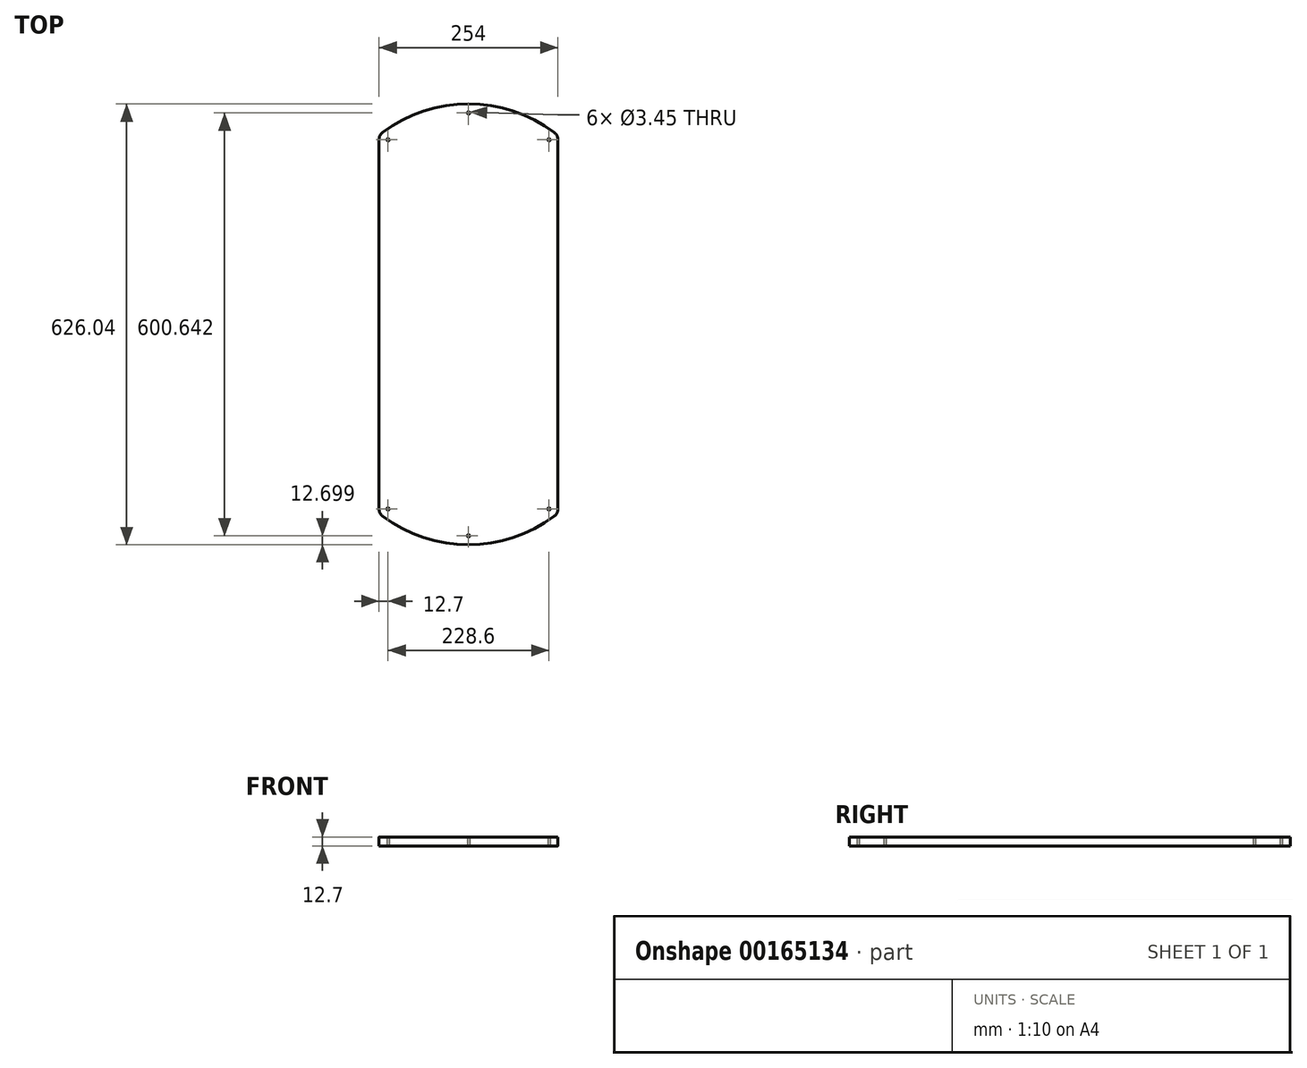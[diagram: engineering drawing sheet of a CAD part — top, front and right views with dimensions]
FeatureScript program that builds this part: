
annotation { "Feature Type Name" : "Feature", "Feature Type Description" : "" }
export const myFeature = defineFeature(function(context is Context, id is Id, definition is map)
    precondition{}
    {
        {
            var Q0;
            Q0=qCreatedBy(makeId("Top.planeOp"),FACE);
            var sketch = newSketch(context, id + "F0", { "sketchPlane" : qUnion([Q0])});
            skLineSegment(sketch, "E0.bottom", {"start": v(127, 262.22) * mm, "end": v(-127, 262.22) * mm, "construction": true});
            skLineSegment(sketch, "E0.top", {"start": v(127, -262.22) * mm, "end": v(-127, -262.22) * mm, "construction": true});
            skLineSegment(sketch, "E0.left", {"start": v(127, 262.22) * mm, "end": v(127, -262.22) * mm});
            skLineSegment(sketch, "E0.right", {"start": v(-127, 262.22) * mm, "end": v(-127, -262.22) * mm});
            skPoint(sketch, "E0.middle", {"position": v(0, 0) * mm});
            skArc(sketch, "E1", {"start": v(121.92, 272.38) * mm, "mid": v(0, 313.02) * mm, "end": v(-121.92, 272.38) * mm});
            skLineSegment(sketch, "E2", {"start": v(0, 262.22) * mm, "end": v(0, 109.82) * mm, "construction": true});
            skLineSegment(sketch, "E3", {"start": v(0, -109.82) * mm, "end": v(0, -262.22) * mm, "construction": true});
            skLineSegment(sketch, "E4", {"start": v(0, 109.82) * mm, "end": v(57.15, 186.02) * mm, "construction": true});
            skLineSegment(sketch, "E5", {"start": v(-57.15, 186.02) * mm, "end": v(0, 109.82) * mm, "construction": true});
            skLineSegment(sketch, "E6", {"start": v(0, 262.22) * mm, "end": v(0, 300.32) * mm, "construction": true});
            skCircle(sketch, "E7", {"center": v(0, 300.32) * mm, "radius": 12.7 * mm, "construction": true});
            skLineSegment(sketch, "E8", {"start": v(0, 186.02) * mm, "end": v(-57.15, 186.02) * mm, "construction": true});
            skLineSegment(sketch, "E9", {"start": v(0, 186.02) * mm, "end": v(57.15, 186.02) * mm, "construction": true});
            skLineSegment(sketch, "E10", {"start": v(-57.15, 186.02) * mm, "end": v(-114.3, 262.22) * mm, "construction": true});
            skLineSegment(sketch, "E11", {"start": v(57.15, 186.02) * mm, "end": v(114.3, 262.22) * mm, "construction": true});
            skCircle(sketch, "E12", {"center": v(-114.3, 262.22) * mm, "radius": 1.73 * mm});
            skCircle(sketch, "E13", {"center": v(114.3, 262.22) * mm, "radius": 1.73 * mm});
            skCircle(sketch, "E14", {"center": v(0, 300.32) * mm, "radius": 1.73 * mm});
            skArc(sketch, "E15", {"start": v(121.92, -272.38) * mm, "mid": v(125.66, -267.9) * mm, "end": v(127, -262.22) * mm});
            skArc(sketch, "E16", {"start": v(-127, -262.22) * mm, "mid": v(-125.66, -267.9) * mm, "end": v(-121.92, -272.38) * mm});
            skArc(sketch, "E17", {"start": v(-121.92, -272.38) * mm, "mid": v(0, -313.02) * mm, "end": v(121.92, -272.38) * mm});
            skArc(sketch, "E18", {"start": v(-121.92, 272.38) * mm, "mid": v(-125.66, 267.9) * mm, "end": v(-127, 262.22) * mm});
            skArc(sketch, "E19", {"start": v(127, 262.22) * mm, "mid": v(125.66, 267.9) * mm, "end": v(121.92, 272.38) * mm});
            skCircle(sketch, "E20", {"center": v(114.3, -262.22) * mm, "radius": 1.73 * mm});
            skCircle(sketch, "E21", {"center": v(-114.3, -262.22) * mm, "radius": 1.73 * mm});
            skLineSegment(sketch, "E22", {"start": v(0, -262.22) * mm, "end": v(0, -300.32) * mm, "construction": true});
            skCircle(sketch, "E23", {"center": v(0, -300.32) * mm, "radius": 12.7 * mm, "construction": true});
            skCircle(sketch, "E24", {"center": v(0, -300.32) * mm, "radius": 1.73 * mm});
            skSolve(sketch);
        }
        {
            var Q0;
            Q0 = qSketchRegion(id + "F0", true);
            extrude(context, id + "F1", {"entities" : qUnion([Q0]), "depth" : 12.7 * mm});
        }
    });
